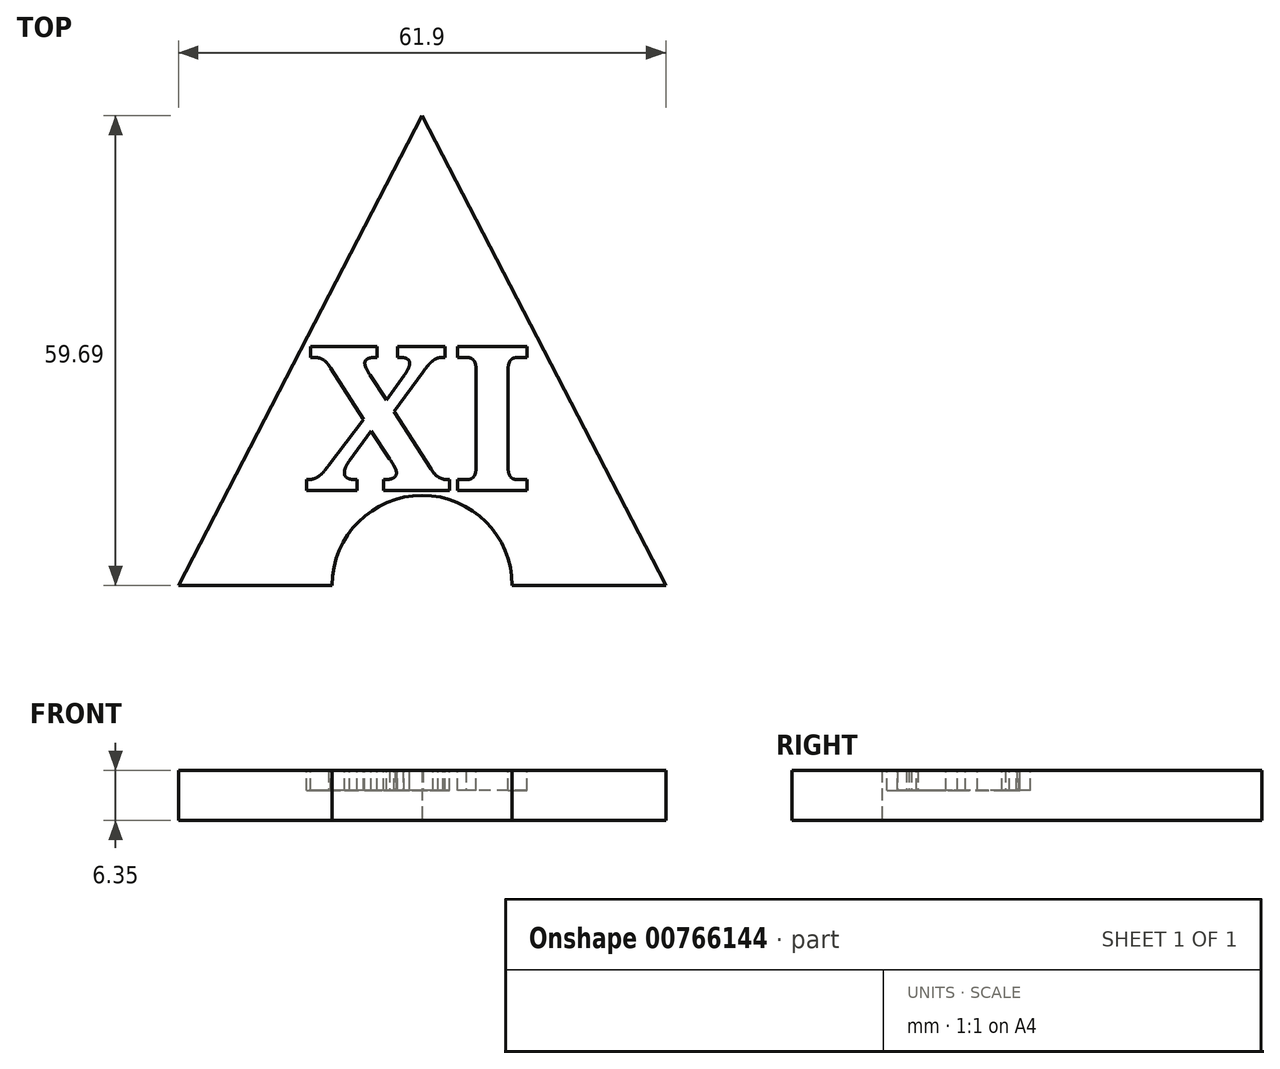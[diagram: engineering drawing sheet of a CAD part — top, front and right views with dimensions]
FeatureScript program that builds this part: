
annotation { "Feature Type Name" : "Feature", "Feature Type Description" : "" }
export const myFeature = defineFeature(function(context is Context, id is Id, definition is map)
    precondition{}
    {
        {
            var Q0;
            Q0=qCreatedBy(makeId("Top.planeOp"),FACE);
            var sketch = newSketch(context, id + "F0", { "sketchPlane" : qUnion([Q0])});
            skCircle(sketch, "E0.cCircle", {"center": v(0, 0.24) * mm, "radius": 17.87 * mm, "construction": true});
            skLineSegment(sketch, "E0.0", {"start": v(30.95, -17.63) * mm, "end": v(-30.95, -17.63) * mm});
            skLineSegment(sketch, "E0.1", {"start": v(-30.95, -17.63) * mm, "end": v(0, 42.06) * mm});
            skLineSegment(sketch, "E0.2", {"start": v(0, 42.06) * mm, "end": v(30.95, -17.63) * mm});
            skPoint(sketch, "E0.0.midPoint", {"position": v(0, -17.63) * mm});
            skSolve(sketch);
        }
        {
            var Q0;
            Q0=makeQuery(id+"F0.imprint","IMPRINT",FACE,{"disambiguationData":[TD([[makeQuery(id+"F0.imprint","IMPRINT",EDGE,{"derivedFrom":sQuery(id+"F0.wireOp",EDGE,"E0.0")}),-1.0]])]});
            extrude(context, id + "F1", {"entities" : qUnion([Q0]), "depth" : 6.35 * mm, "offsetDistance" : 25.4 * mm});
        }
        {
            var Q0;
            Q0=sQuery(id+"F0.wireOp",VERTEX,"E0.0.midPoint");
            var Q1;
            Q1=makeQuery(id+"F1.opExtrude","SWEPT_BODY",BODY,{"disambiguationData":[OSD([sQuery(id+"F0.wireOp",EDGE,"E0.0"),sQuery(id+"F0.wireOp",EDGE,"E0.1"),sQuery(id+"F0.wireOp",EDGE,"E0.2")])]});
            hole(context, id + "F2", {"style" : HoleStyle.SIMPLE, "endStyle" : HoleEndStyle.THROUGH, "oppositeDirection" : true, "holeDiameter" : 22.86 * mm, "majorDiameter" : 6.35 * mm, "isTappedThrough" : true, "tappedDepth" : 12.7 * mm, "tapClearance" : 3, "locations" : qUnion([Q0]), "scope" : qUnion([Q1])});
        }
        {
            var Q0;
            Q0=makeQuery(id+"F1.opExtrude","CAP_FACE",FACE,{"disambiguationData":[OSD([sQuery(id+"F0.wireOp",EDGE,"E0.0"),sQuery(id+"F0.wireOp",EDGE,"E0.1"),sQuery(id+"F0.wireOp",EDGE,"E0.2")])],"isStart":false});
            var sketch = newSketch(context, id + "F3", { "sketchPlane" : qUnion([Q0])});
            skText(sketch, "E1", { "text": "XI", "fontName": "NotoSerif-Bold.ttf"});
            const initialGuessF3  = {"E1": [-0.01496, -0.00556, 1, 0, 0.01841]};
            skSetInitialGuess(sketch, initialGuessF3);
            skSolve(sketch);
        }
        {
            var Q0;
            Q0 = qSketchRegion(id + "F3", true);
            extrude(context, id + "F4", {"entities" : qUnion([Q0]), "operationType" : NewBodyOperationType.REMOVE, "oppositeDirection" : true, "depth" : 2.54 * mm, "offsetDistance" : 25.4 * mm});
        }
    });
